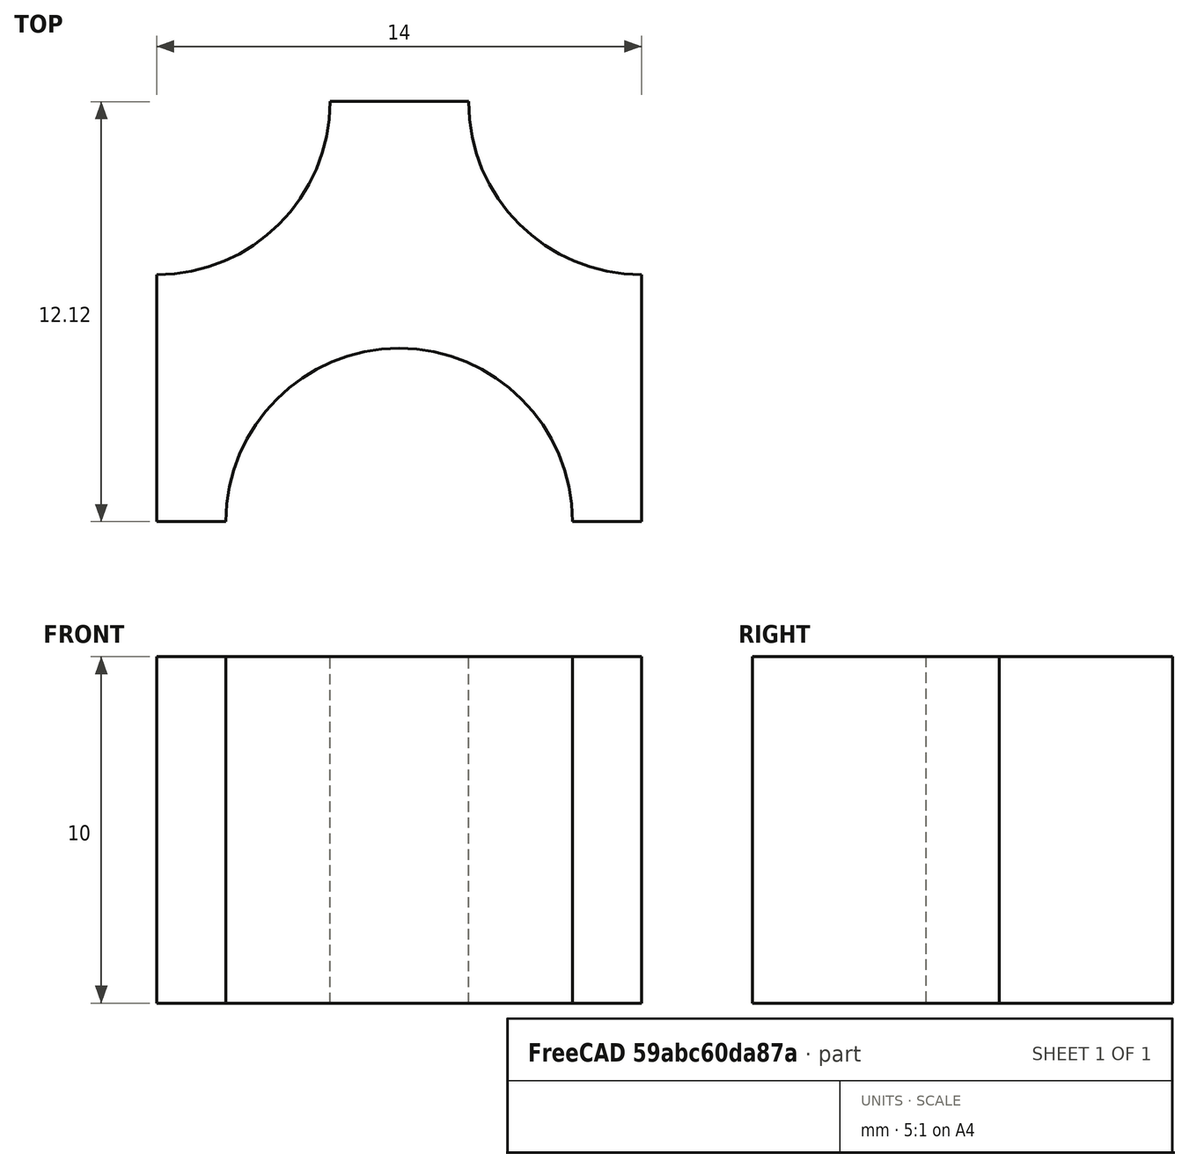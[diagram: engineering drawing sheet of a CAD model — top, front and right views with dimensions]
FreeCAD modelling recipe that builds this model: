
FCSTD DOCUMENT  (FreeCAD 1.1R20260325 (Git shallow))
Label: periodic_boundary_meanvelocityforce
License: All rights reserved
LicenseURL: https://en.wikipedia.org/wiki/All_rights_reserved
objects: App::Point×1, Sketcher::SketchObject×1, PartDesign::Pad×1, PartDesign::Body×1
note: 6 computed .brp shape members not serialized (recipe doc carries the construction recipe); baked Part::Feature solids carry a one-line shape summary decoded from their .brp

FEATURE [App::Point] Origin001
  Role = Origin
FEATURE [Sketcher::SketchObject] Sketch
  ArcFitTolerance = 1e-06
  AttachmentSupport = -> [XY_Plane]
  ExternalTypes = [0]
  FullyConstrained = true
  MakeInternals = false
  MapMode = 5
  _ExternalGeoVersion = 0
  sketch-geometry (15):
    g0: ArcOfCircle CenterX=0 CenterY=0 CenterZ=0 NormalX=0 NormalY=0 NormalZ=1 AngleXU=0 Radius=5 StartAngle=0 EndAngle=3.14159
    g1: ArcOfCircle CenterX=-7 CenterY=12.1244 CenterZ=0 NormalX=0 NormalY=0 NormalZ=1 AngleXU=0 Radius=5 StartAngle=4.71239 EndAngle=6.28319
    g2: ArcOfCircle CenterX=7 CenterY=12.1244 CenterZ=0 NormalX=0 NormalY=0 NormalZ=1 AngleXU=0 Radius=5 StartAngle=3.14159 EndAngle=4.71239
    g3: LineSegment StartX=-7 StartY=7.12436 StartZ=0 EndX=-7 EndY=9e-16 EndZ=0
    g4: LineSegment StartX=-7 StartY=9e-16 StartZ=0 EndX=-5 EndY=9e-16 EndZ=0
    g5: LineSegment StartX=7 StartY=0 StartZ=0 EndX=7 EndY=7.12436 EndZ=0
    g6: LineSegment StartX=2 StartY=12.1244 StartZ=0 EndX=-2 EndY=12.1244 EndZ=0
    g7: LineSegment [constr] StartX=9e-16 StartY=0 StartZ=0 EndX=7 EndY=12.1244 EndZ=0
    g8: LineSegment [constr] StartX=7 StartY=12.1244 StartZ=0 EndX=-7 EndY=12.1244 EndZ=0
    g9: LineSegment [constr] StartX=-7 StartY=12.1244 StartZ=0 EndX=9e-16 EndY=0 EndZ=0
    g10: Circle [constr] CenterX=0 CenterY=8.0829 CenterZ=0 NormalX=0 NormalY=0 NormalZ=1 AngleXU=0 Radius=8.0829
    g11: LineSegment [constr] StartX=-7 StartY=7.12436 StartZ=0 EndX=-7 EndY=12.1244 EndZ=0
    g12: LineSegment [constr] StartX=7 StartY=7.12436 StartZ=0 EndX=7 EndY=12.1244 EndZ=0
    g13: LineSegment StartX=5 StartY=0 StartZ=0 EndX=7 EndY=0 EndZ=0
    g14: GeomPoint [constr] X=0 Y=12.1244 Z=0
  constraints (42):
    c: Coincident(g0,g-1)
    c: Diameter(g0) = 10
    c: Coincident(g3,g4)
    c: Coincident(g13,g5)
    c: Vertical(g3)
    c: Vertical(g5)
    c: Horizontal(g6)
    c: PointOnObject(g13,g-1)
    c: Equal(g2,g1)
    c: Equal(g1,g0)
    c: Coincident(g7,g8)
    c: Coincident(g8,g9)
    c: Coincident(g9,g7)
    c: Equal(g7,g8)
    c: Equal(g7,g9)
    c: PointOnObject(g7,g10)
    c: PointOnObject(g8,g10)
    c: PointOnObject(g9,g10)
    c: PointOnObject(g10,g-2)
    c: Symmetric(g4,g13,g9)
    c: Coincident(g1,g8)
    c: PointOnObject(g2,g8)
    c: Coincident(g2,g5)
    c: PointOnObject(g0,g13)
    c: Coincident(g3,g1)
    c: Coincident(g11,g1)
    c: Coincident(g11,g1)
    c: Vertical(g11)
    c: Coincident(g12,g2)
    c: Coincident(g12,g2)
    c: Vertical(g12)
    c: Coincident(g1,g6)
    c: PointOnObject(g13,g0)
    c: Coincident(g4,g0)
    c: Horizontal(g4)
    c: Coincident(g2,g6)
    c: Symmetric(g6,g6,g14)
    c: PointOnObject(g14,g-2)
    c: PointOnObject(g3,g-1)
    c: Equal(g5,g3)
    c: Horizontal(g13)
    c: DistanceX(g1,g2) = 14
FEATURE [PartDesign::Pad] Pad
  Direction = (0,0,1)
  Length = 10
  Length2 = 10
  Profile = -> Sketch
  ReferenceAxis = -> Sketch [N_Axis]
  Refine = true
  SideType = 0
  Suppressed = false
  Type = 0
  Type2 = 0
FEATURE [PartDesign::Body] Body
  AllowCompound = true
  Group = -> [Sketch,Pad]
  Origin = -> Origin
  Tip = -> Pad
